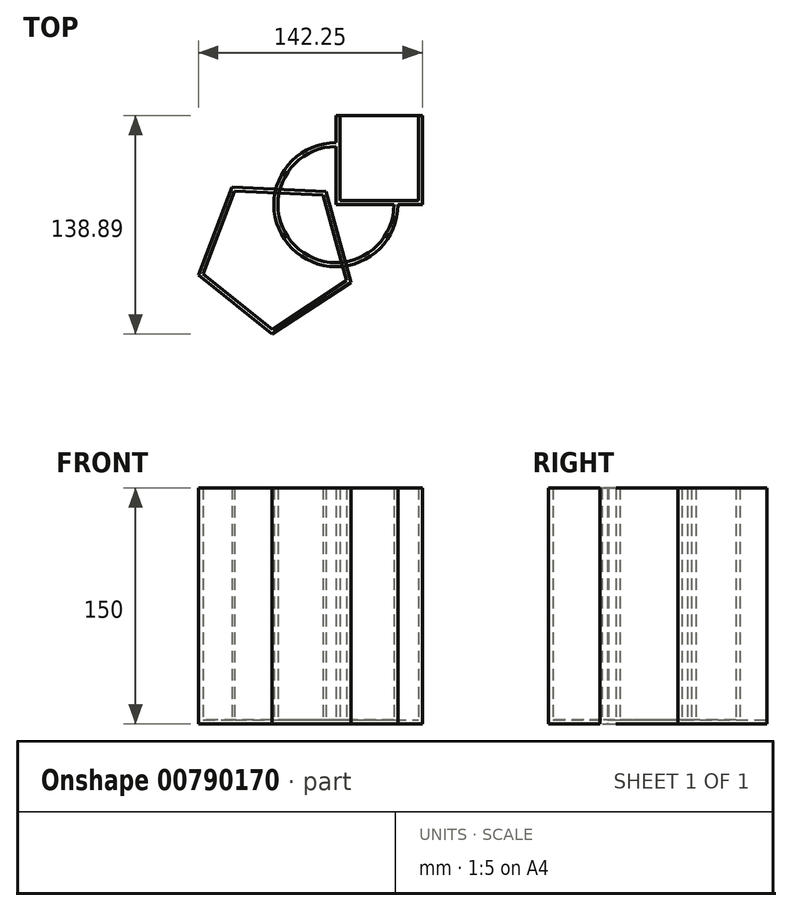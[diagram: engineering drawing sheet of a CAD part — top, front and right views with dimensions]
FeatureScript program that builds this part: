
annotation { "Feature Type Name" : "Feature", "Feature Type Description" : "" }
export const myFeature = defineFeature(function(context is Context, id is Id, definition is map)
    precondition{}
    {
        {
            var Q0;
            Q0=qCreatedBy(makeId("Top.planeOp"),FACE);
            var sketch = newSketch(context, id + "F0", { "sketchPlane" : qUnion([Q0])});
            skCircle(sketch, "E0", {"center": v(0, 0) * mm, "radius": 39.39 * mm});
            skSolve(sketch);
        }
        {
            var Q0;
            Q0=makeQuery(id+"F0.imprint","IMPRINT",FACE,{"disambiguationData":[TD([[makeQuery(id+"F0.imprint","IMPRINT",EDGE,{"derivedFrom":sQuery(id+"F0.wireOp",EDGE,"E0")}),1.0]])]});
            extrude(context, id + "F1", {"entities" : qUnion([Q0]), "depth" : 150 * mm, "offsetDistance" : 25 * mm});
        }
        {
            var Q0;
            Q0=makeQuery(id+"F1.opExtrude","CAP_FACE",FACE,{"disambiguationData":[OSD([sQuery(id+"F0.wireOp",EDGE,"E0")])],"isStart":false});
            var Q1;
            Q1=makeQuery(id+"F1.opExtrude","SWEPT_BODY",BODY,{"disambiguationData":[OSD([sQuery(id+"F0.wireOp",EDGE,"E0")])]});
            shell(context, id + "F2", {"entities" : qUnion([Q0]), "parts" : qUnion([Q1]), "thickness" : 2.5 * mm});
        }
        {
            var Q0;
            Q0=qCreatedBy(makeId("Top.planeOp"),FACE);
            var sketch = newSketch(context, id + "F3", { "sketchPlane" : qUnion([Q0])});
            skLineSegment(sketch, "E1.bottom", {"start": v(0, 0) * mm, "end": v(54.89, 0) * mm});
            skLineSegment(sketch, "E1.top", {"start": v(0, 56.54) * mm, "end": v(54.89, 56.54) * mm});
            skLineSegment(sketch, "E1.left", {"start": v(0, 0) * mm, "end": v(0, 56.54) * mm});
            skLineSegment(sketch, "E1.right", {"start": v(54.89, 0) * mm, "end": v(54.89, 56.54) * mm});
            skSolve(sketch);
        }
        {
            var Q0;
            Q0=makeQuery(id+"F3.imprint","IMPRINT",FACE,{"disambiguationData":[TD([[makeQuery(id+"F3.imprint","IMPRINT",EDGE,{"derivedFrom":sQuery(id+"F3.wireOp",EDGE,"E1.bottom")}),1.0]])]});
            extrude(context, id + "F4", {"entities" : qUnion([Q0]), "operationType" : NewBodyOperationType.ADD, "depth" : 150 * mm, "offsetDistance" : 25 * mm});
        }
        {
            var Q0;
            Q0=makeQuery(id+"F4.opExtrude","SWEPT_FACE",FACE,{"disambiguationData":[OSD([sQuery(id+"F3.wireOp",EDGE,"E1.top")])]});
            var Q1;
            Q1=makeQuery(id+"F4.boolean.opBoolean","MERGE",FACE,{"derivedFrom":[makeQuery(id+"F1.opExtrude","CAP_FACE",FACE,{"disambiguationData":[OSD([sQuery(id+"F0.wireOp",EDGE,"E0")])],"isStart":false}),makeQuery(id+"F4.opExtrude","CAP_FACE",FACE,{"disambiguationData":[OSD([sQuery(id+"F3.wireOp",EDGE,"E1.bottom"),sQuery(id+"F3.wireOp",EDGE,"E1.top"),sQuery(id+"F3.wireOp",EDGE,"E1.left"),sQuery(id+"F3.wireOp",EDGE,"E1.right")])],"isStart":false})]});
            shell(context, id + "F5", {"entities" : qUnion([Q0, Q1]), "thickness" : 2.5 * mm});
        }
        {
            var Q0;
            Q0=qCreatedBy(makeId("Top.planeOp"),FACE);
            var sketch = newSketch(context, id + "F6", { "sketchPlane" : qUnion([Q0])});
            skCircle(sketch, "E2.cCircle", {"center": v(-38.14, -31.38) * mm, "radius": 41.28 * mm, "construction": true});
            skLineSegment(sketch, "E2.0", {"start": v(-40.55, -82.35) * mm, "end": v(-87.36, -44.84) * mm});
            skLineSegment(sketch, "E2.1", {"start": v(-87.36, -44.84) * mm, "end": v(-66.15, 11.27) * mm});
            skLineSegment(sketch, "E2.2", {"start": v(-66.15, 11.27) * mm, "end": v(-6.23, 8.44) * mm});
            skLineSegment(sketch, "E2.3", {"start": v(-6.23, 8.44) * mm, "end": v(9.6, -49.42) * mm});
            skLineSegment(sketch, "E2.4", {"start": v(9.6, -49.42) * mm, "end": v(-40.55, -82.35) * mm});
            skPoint(sketch, "E2.0.midPoint", {"position": v(-63.95, -63.6) * mm});
            skSolve(sketch);
        }
        {
            var Q0;
            Q0 = qSketchRegion(id + "F6", true);
            extrude(context, id + "F7", {"entities" : qUnion([Q0]), "depth" : 150 * mm, "offsetDistance" : 25 * mm});
        }
        {
            var Q0;
            Q0=makeQuery(id+"F7.opExtrude","CAP_FACE",FACE,{"disambiguationData":[OSD([sQuery(id+"F6.wireOp",EDGE,"E2.0"),sQuery(id+"F6.wireOp",EDGE,"E2.1"),sQuery(id+"F6.wireOp",EDGE,"E2.2"),sQuery(id+"F6.wireOp",EDGE,"E2.3"),sQuery(id+"F6.wireOp",EDGE,"E2.4")])],"isStart":false});
            shell(context, id + "F8", {"entities" : qUnion([Q0]), "thickness" : 2.5 * mm});
        }
    });
